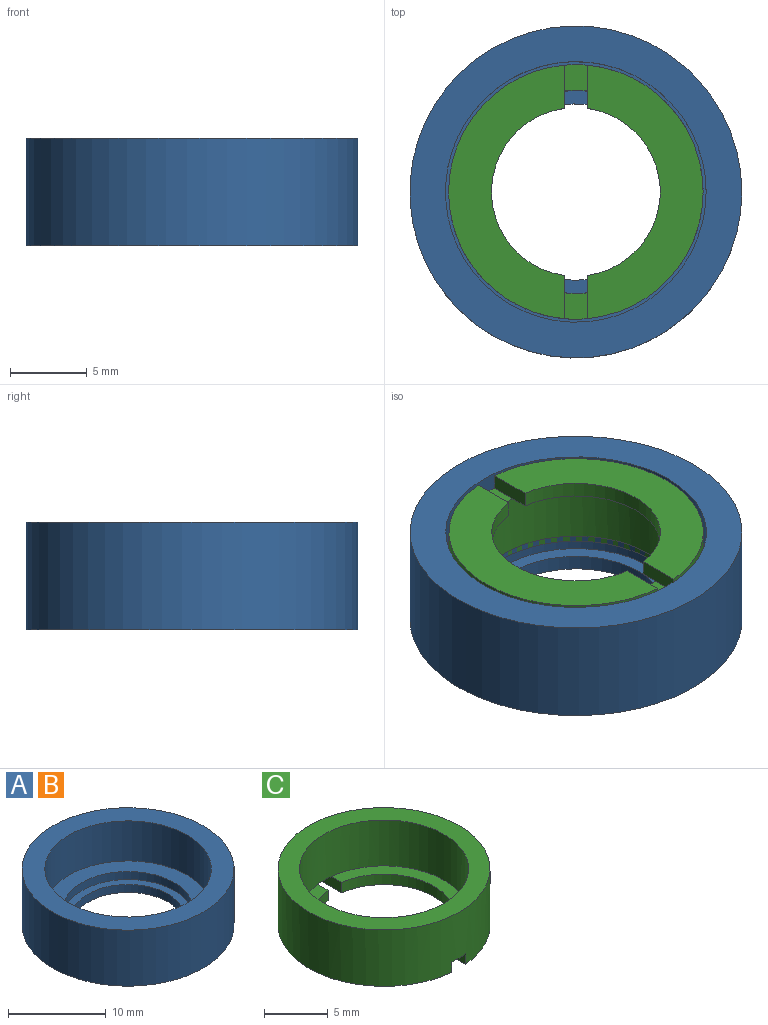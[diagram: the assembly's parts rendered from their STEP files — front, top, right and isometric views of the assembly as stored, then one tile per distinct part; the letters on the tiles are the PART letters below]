
ASSEMBLY  parts=3 mates=1
PART A: 8 faces, bbox 21.7x21.7x7 mm
  f0: plane 17x17mm, normal (0,0,1), area 89.1mm2, adj f5,f6
  f1: plane 13.25x13.25mm, normal (0,0,1), area 34mm2, adj f2,f5
  f2: cylinder r=5.75mm len=11.5mm, axis (0,0,-1), area 36.1mm2, adj f1,f4
  f3: cylinder r=10.82mm len=21.65mm, axis (0,0,-1), area 476.1mm2, adj f4,f7
  f4: plane 21.65x21.65mm, normal (0,0,-1), area 264.3mm2, adj f2,f3
  f5: cylinder r=6.62mm len=13.25mm, axis (0,0,-1), area 41.6mm2, adj f0,f1
  f6: cylinder r=8.5mm len=17mm, axis (0,0,-1), area 267mm2, adj f0,f7
  f7: plane 21.65x21.65mm, normal (0,0,1), area 141.2mm2, adj f3,f6
PART B: same geometry as A
PART C: 15 faces, bbox 16.6x16.6x5.4 mm
  f0: plane 13.17x5.88mm, normal (0,0,1), area 19.7mm2, adj f2,f7,f10,f13
  f1: cylinder r=5.5mm len=10.9mm, axis (0,0,-1), area 15.8mm2, adj f3,f5,f11,f14
  f2: cylinder r=5.5mm len=10.9mm, axis (0,0,-1), area 15.8mm2, adj f0,f4,f10,f13
  f3: plane 16.53x7.55mm, normal (0,0,-1), area 56.5mm2, adj f1,f6,f11,f14
  f4: plane 16.53x7.55mm, normal (0,0,-1), area 56.5mm2, adj f2,f6,f10,f13
  f5: plane 13.17x5.88mm, normal (0,0,1), area 19.7mm2, adj f1,f7,f11,f14
  f6: cylinder r=8.3mm len=16.6mm, axis (0,0,-1), area 278.6mm2, adj f3,f4,f8,f9,f10,f11,f12,f13
  f7: cylinder r=6.62mm len=13.25mm, axis (0,0,-1), area 183.2mm2, adj f0,f5,f8,f9,f12
  f8: plane 16.6x16.6mm, normal (0,0,1), area 78.5mm2, adj f6,f7
  f9: plane 1.72x1.5mm, normal (0,0,-1), area 2.5mm2, adj f6,f7,f10,f11
  f10: plane 2.82x1mm, normal (-1,0,0), area 2.8mm2, adj f0,f2,f4,f6,f9
  f11: plane 2.82x1mm, normal (1,0,0), area 2.8mm2, adj f1,f3,f5,f6,f9
  f12: plane 1.72x1.5mm, normal (0,0,-1), area 2.5mm2, adj f6,f7,f13,f14
  f13: plane 2.82x1mm, normal (-1,0,0), area 2.8mm2, adj f0,f2,f4,f6,f12
  f14: plane 2.82x1mm, normal (1,0,0), area 2.8mm2, adj f1,f3,f5,f6,f12
PLACE A t=(-1.26,1.48,-0.19)mm
PLACE B t=(-1.26,1.48,-0.19)mm
PLACE C rot(axis=(0,1,0),180deg) t=(30.88,1.48,6.81)mm
MATE planar C.f1 <-> A.f3  axis (0,0,1) through (-1.26,1.48,6.81)mm
